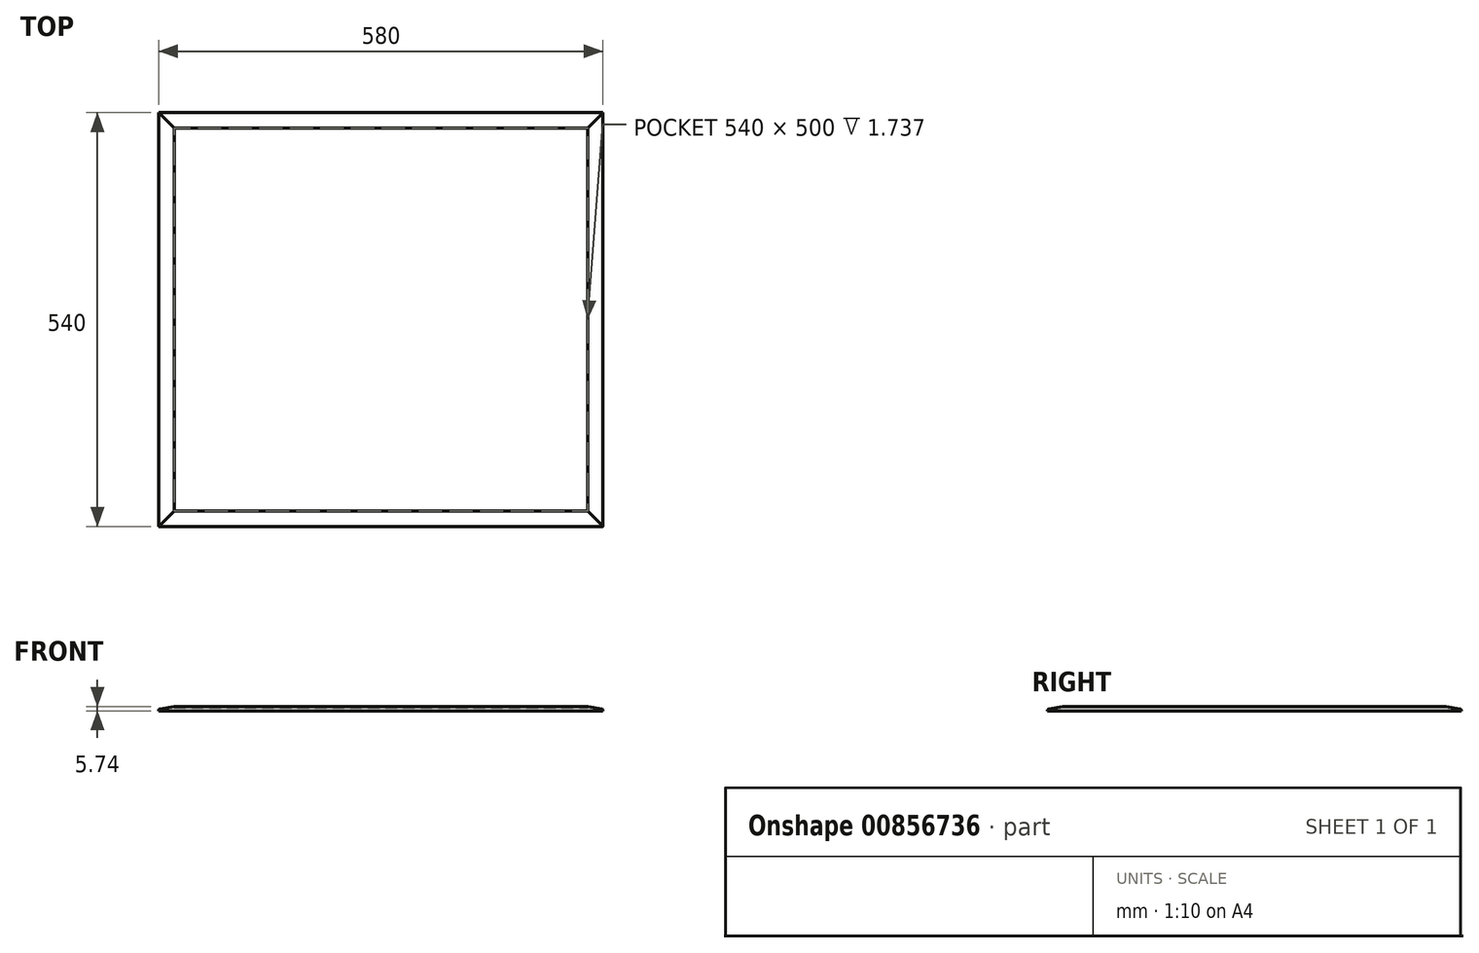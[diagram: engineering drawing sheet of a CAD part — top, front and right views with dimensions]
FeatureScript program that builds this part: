
annotation { "Feature Type Name" : "Feature", "Feature Type Description" : "" }
export const myFeature = defineFeature(function(context is Context, id is Id, definition is map)
    precondition{}
    {
        {
            var Q0;
            Q0=qCreatedBy(makeId("Top.planeOp"),FACE);
            var sketch = newSketch(context, id + "F0", { "sketchPlane" : qUnion([Q0])});
            skLineSegment(sketch, "E0.bottom", {"start": v(-291.46, 264.16) * mm, "end": v(288.54, 264.16) * mm});
            skLineSegment(sketch, "E0.top", {"start": v(-291.46, -275.84) * mm, "end": v(288.54, -275.84) * mm});
            skLineSegment(sketch, "E0.left", {"start": v(-291.46, 264.16) * mm, "end": v(-291.46, -275.84) * mm});
            skLineSegment(sketch, "E0.right", {"start": v(288.54, 264.16) * mm, "end": v(288.54, -275.84) * mm});
            skSolve(sketch);
        }
        {
            var Q0;
            Q0=makeQuery(id+"F0.imprint","IMPRINT",FACE,{"disambiguationData":[TD([[makeQuery(id+"F0.imprint","IMPRINT",EDGE,{"derivedFrom":sQuery(id+"F0.wireOp",EDGE,"E0.bottom")}),-1.0]])]});
            extrude(context, id + "F1", {"entities" : qUnion([Q0]), "depth" : 7.5 * mm, "offsetDistance" : 25 * mm});
        }
        {
            var Q0;
            Q0=makeQuery(id+"F1.opExtrude","CAP_FACE",FACE,{"disambiguationData":[OSD([sQuery(id+"F0.wireOp",EDGE,"E0.bottom"),sQuery(id+"F0.wireOp",EDGE,"E0.top"),sQuery(id+"F0.wireOp",EDGE,"E0.left"),sQuery(id+"F0.wireOp",EDGE,"E0.right")])],"isStart":false});
            var Q1;
            Q1=makeQuery(id+"F1.opExtrude","CAP_FACE",FACE,{"disambiguationData":[OSD([sQuery(id+"F0.wireOp",EDGE,"E0.bottom"),sQuery(id+"F0.wireOp",EDGE,"E0.top"),sQuery(id+"F0.wireOp",EDGE,"E0.left"),sQuery(id+"F0.wireOp",EDGE,"E0.right")])],"isStart":true});
            shell(context, id + "F2", {"entities" : qUnion([Q0, Q1]), "thickness" : 20 * mm});
        }
        {
            var Q0;
            Q0=makeQuery(id+"F1.opExtrude","CAP_EDGE",EDGE,{"disambiguationData":[OSD([sQuery(id+"F0.wireOp",EDGE,"E0.left")])],"isStart":false});
            var Q1;
            Q1=makeQuery(id+"F1.opExtrude","CAP_EDGE",EDGE,{"disambiguationData":[OSD([sQuery(id+"F0.wireOp",EDGE,"E0.top")])],"isStart":false});
            var Q2;
            Q2=makeQuery(id+"F1.opExtrude","CAP_EDGE",EDGE,{"disambiguationData":[OSD([sQuery(id+"F0.wireOp",EDGE,"E0.right")])],"isStart":false});
            var Q3;
            Q3=makeQuery(id+"F1.opExtrude","CAP_EDGE",EDGE,{"disambiguationData":[OSD([sQuery(id+"F0.wireOp",EDGE,"E0.bottom")])],"isStart":false});
            chamfer(context, id + "F3", {"entities" : qUnion([Q0, Q1, Q2, Q3]), "chamferType" : ChamferType.OFFSET_ANGLE, "width" : 30 * mm, "oppositeDirection" : false, "angle" : 10 * degree, "tangentPropagation" : true});
        }
        {
            var Q0;
            {var subQ0=sQuery(id+"F0.wireOp",EDGE,"E0.left");Q0=makeQuery(id+"F3.opChamfer","BLEND_EDGE",EDGE,{"blendedFrom":[makeQuery(id+"F1.opExtrude","CAP_EDGE",EDGE,{"disambiguationData":[OSD([subQ0])],"isStart":false}),makeQuery(id+"F1.opExtrude","SWEPT_FACE",FACE,{"disambiguationData":[OSD([subQ0])]})],"blendedInto":[makeQuery(id+"F1.opExtrude","SWEPT_FACE",FACE,{"disambiguationData":[OSD([subQ0])]})]});}
            var Q1;
            {var subQ0=sQuery(id+"F0.wireOp",EDGE,"E0.top");Q1=makeQuery(id+"F3.opChamfer","BLEND_EDGE",EDGE,{"blendedFrom":[makeQuery(id+"F1.opExtrude","CAP_EDGE",EDGE,{"disambiguationData":[OSD([subQ0])],"isStart":false}),makeQuery(id+"F1.opExtrude","SWEPT_FACE",FACE,{"disambiguationData":[OSD([subQ0])]})],"blendedInto":[makeQuery(id+"F1.opExtrude","SWEPT_FACE",FACE,{"disambiguationData":[OSD([subQ0])]})]});}
            var Q2;
            {var subQ0=sQuery(id+"F0.wireOp",EDGE,"E0.right");Q2=makeQuery(id+"F3.opChamfer","BLEND_EDGE",EDGE,{"blendedFrom":[makeQuery(id+"F1.opExtrude","CAP_EDGE",EDGE,{"disambiguationData":[OSD([subQ0])],"isStart":false}),makeQuery(id+"F1.opExtrude","SWEPT_FACE",FACE,{"disambiguationData":[OSD([subQ0])]})],"blendedInto":[makeQuery(id+"F1.opExtrude","SWEPT_FACE",FACE,{"disambiguationData":[OSD([subQ0])]})]});}
            var Q3;
            {var subQ0=sQuery(id+"F0.wireOp",EDGE,"E0.bottom");Q3=makeQuery(id+"F3.opChamfer","BLEND_EDGE",EDGE,{"blendedFrom":[makeQuery(id+"F1.opExtrude","CAP_EDGE",EDGE,{"disambiguationData":[OSD([subQ0])],"isStart":false}),makeQuery(id+"F1.opExtrude","SWEPT_FACE",FACE,{"disambiguationData":[OSD([subQ0])]})],"blendedInto":[makeQuery(id+"F1.opExtrude","SWEPT_FACE",FACE,{"disambiguationData":[OSD([subQ0])]})]});}
            fillet(context, id + "F4", {"entities" : qUnion([Q0, Q1, Q2, Q3]), "radius" : 2 * mm, "tangentPropagation" : true, "allowEdgeOverflow" : false});
        }
        {
            var Q0;
            Q0=qCreatedBy(makeId("Top.planeOp"),FACE);
            var sketch = newSketch(context, id + "F5", { "sketchPlane" : qUnion([Q0])});
            skLineSegment(sketch, "E1.bottom", {"start": v(-271.46, 244.16) * mm, "end": v(268.54, 244.16) * mm});
            skLineSegment(sketch, "E1.top", {"start": v(-271.46, -255.84) * mm, "end": v(268.54, -255.84) * mm});
            skLineSegment(sketch, "E1.left", {"start": v(-271.46, 244.16) * mm, "end": v(-271.46, -255.84) * mm});
            skLineSegment(sketch, "E1.right", {"start": v(268.54, 244.16) * mm, "end": v(268.54, -255.84) * mm});
            skSolve(sketch);
        }
        {
            var Q0;
            Q0 = qSketchRegion(id + "F5", true);
            extrude(context, id + "F6", {"entities" : qUnion([Q0]), "operationType" : NewBodyOperationType.ADD, "depth" : 4 * mm, "offsetDistance" : 25 * mm});
        }
    });
